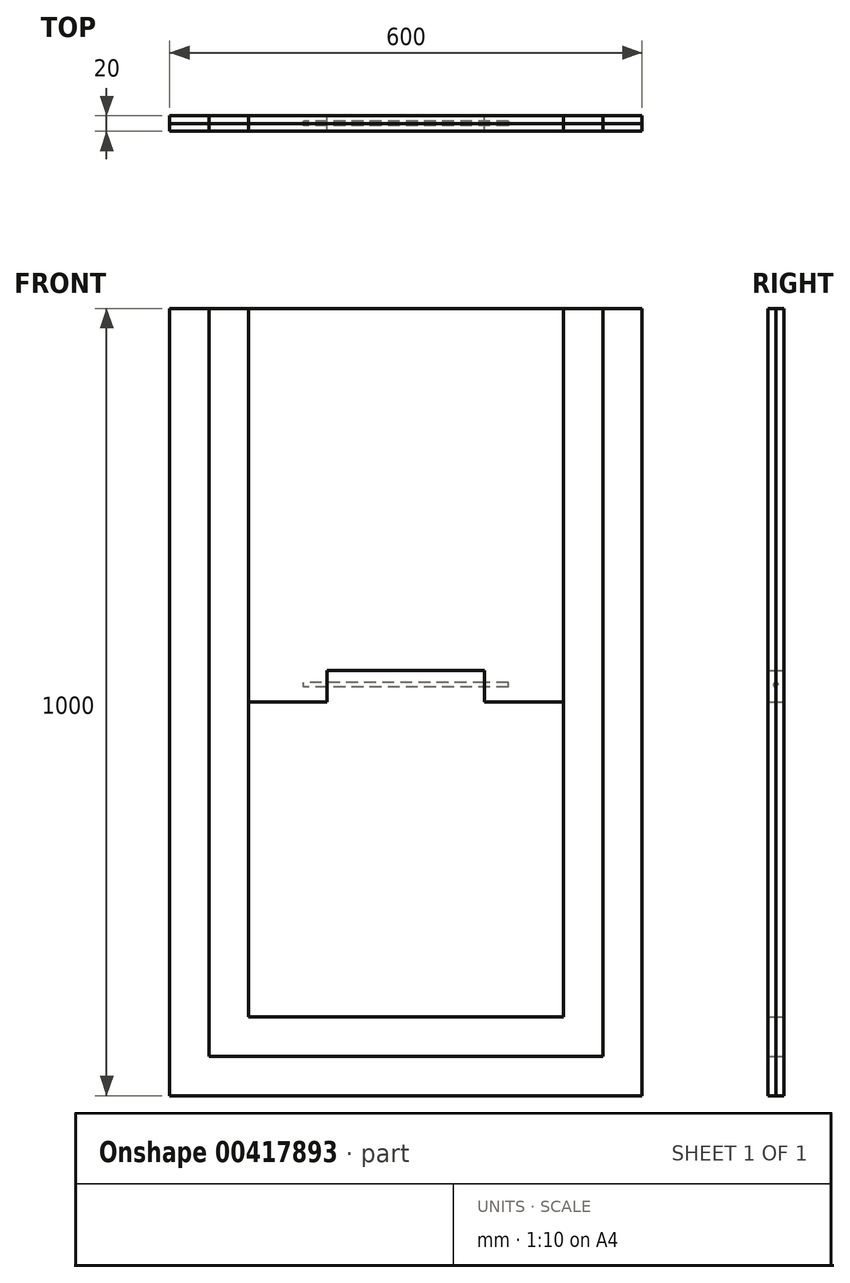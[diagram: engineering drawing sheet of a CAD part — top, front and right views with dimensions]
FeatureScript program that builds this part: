
annotation { "Feature Type Name" : "Feature", "Feature Type Description" : "" }
export const myFeature = defineFeature(function(context is Context, id is Id, definition is map)
    precondition{}
    {
        {
            var Q0;
            Q0=qCreatedBy(makeId("Front.planeOp"),FACE);
            var sketch = newSketch(context, id + "F0", { "sketchPlane" : qUnion([Q0])});
            skLineSegment(sketch, "E0", {"start": v(0, 0) * mm, "end": v(0, 1000) * mm});
            skLineSegment(sketch, "E1", {"start": v(0, 1000) * mm, "end": v(50, 1000) * mm});
            skLineSegment(sketch, "E2", {"start": v(50, 1000) * mm, "end": v(50, 50) * mm});
            skLineSegment(sketch, "E3", {"start": v(50, 50) * mm, "end": v(550, 50) * mm});
            skLineSegment(sketch, "E4", {"start": v(550, 50) * mm, "end": v(550, 1000) * mm});
            skLineSegment(sketch, "E5", {"start": v(550, 1000) * mm, "end": v(600, 1000) * mm});
            skLineSegment(sketch, "E6", {"start": v(600, 1000) * mm, "end": v(600, 0) * mm});
            skLineSegment(sketch, "E7", {"start": v(600, 0) * mm, "end": v(0, 0) * mm});
            skSolve(sketch);
        }
        {
            var Q0;
            Q0=qCreatedBy(makeId("Front.planeOp"),FACE);
            var sketch = newSketch(context, id + "F1", { "sketchPlane" : qUnion([Q0])});
            skLineSegment(sketch, "E8", {"start": v(50, 1000) * mm, "end": v(50, 50) * mm});
            skLineSegment(sketch, "E9", {"start": v(50, 50) * mm, "end": v(550, 50) * mm});
            skLineSegment(sketch, "E10", {"start": v(550, 50) * mm, "end": v(550, 1000) * mm});
            skLineSegment(sketch, "E11", {"start": v(550, 1000) * mm, "end": v(500, 1000) * mm});
            skLineSegment(sketch, "E12", {"start": v(500, 1000) * mm, "end": v(500, 100) * mm});
            skLineSegment(sketch, "E13", {"start": v(500, 100) * mm, "end": v(100, 100) * mm});
            skLineSegment(sketch, "E14", {"start": v(100, 100) * mm, "end": v(100, 1000) * mm});
            skLineSegment(sketch, "E15", {"start": v(100, 1000) * mm, "end": v(50, 1000) * mm});
            skSolve(sketch);
        }
        {
            var Q0;
            Q0=qCreatedBy(makeId("Front.planeOp"),FACE);
            var sketch = newSketch(context, id + "F2", { "sketchPlane" : qUnion([Q0])});
            skLineSegment(sketch, "E16", {"start": v(100, 1000) * mm, "end": v(100, 500) * mm});
            skLineSegment(sketch, "E17", {"start": v(100, 500) * mm, "end": v(200, 500) * mm});
            skLineSegment(sketch, "E18", {"start": v(200, 540) * mm, "end": v(400, 540) * mm});
            skLineSegment(sketch, "E19", {"start": v(400, 500) * mm, "end": v(500, 500) * mm});
            skLineSegment(sketch, "E20", {"start": v(500, 500) * mm, "end": v(500, 1000) * mm});
            skLineSegment(sketch, "E21", {"start": v(500, 1000) * mm, "end": v(100, 1000) * mm});
            skLineSegment(sketch, "E22", {"start": v(200, 500) * mm, "end": v(200, 540) * mm});
            skLineSegment(sketch, "E23", {"start": v(400, 500) * mm, "end": v(400, 540) * mm});
            skLineSegment(sketch, "E24", {"start": v(300, 611.08) * mm, "end": v(300, 468.28) * mm, "construction": true});
            skSolve(sketch);
        }
        {
            var Q0;
            Q0=qCreatedBy(makeId("Front.planeOp"),FACE);
            var sketch = newSketch(context, id + "F3", { "sketchPlane" : qUnion([Q0])});
            skLineSegment(sketch, "E25", {"start": v(200, 460) * mm, "end": v(200, 500) * mm, "construction": true});
            skLineSegment(sketch, "E26", {"start": v(200, 500) * mm, "end": v(100, 500) * mm});
            skLineSegment(sketch, "E27", {"start": v(100, 500) * mm, "end": v(100, 100) * mm});
            skLineSegment(sketch, "E28", {"start": v(100, 100) * mm, "end": v(500, 100) * mm});
            skLineSegment(sketch, "E29", {"start": v(500, 100) * mm, "end": v(500, 500) * mm});
            skLineSegment(sketch, "E30", {"start": v(500, 500) * mm, "end": v(400, 500) * mm});
            skLineSegment(sketch, "E31", {"start": v(400, 500) * mm, "end": v(400, 460) * mm, "construction": true});
            skLineSegment(sketch, "E32", {"start": v(400, 460) * mm, "end": v(200, 460) * mm, "construction": true});
            skLineSegment(sketch, "E33", {"start": v(300, 460) * mm, "end": v(300, 536.5) * mm, "construction": true});
            skLineSegment(sketch, "E34", {"start": v(200, 498) * mm, "end": v(400, 498) * mm, "construction": true});
            skLineSegment(sketch, "E35", {"start": v(200, 478) * mm, "end": v(400, 478) * mm, "construction": true});
            skLineSegment(sketch, "E36.MirrorCS", {"start": v(200, 522) * mm, "end": v(480, 522) * mm, "construction": true});
            skLineSegment(sketch, "E37.MirrorCS", {"start": v(200, 502) * mm, "end": v(400, 502) * mm, "construction": true});
            skLineSegment(sketch, "E38.MirrorCS", {"start": v(400, 500) * mm, "end": v(400, 540) * mm});
            skLineSegment(sketch, "E39.MirrorCS", {"start": v(400, 540) * mm, "end": v(200, 540) * mm});
            skLineSegment(sketch, "E40.MirrorCS", {"start": v(200, 540) * mm, "end": v(200, 500) * mm});
            skSolve(sketch);
        }
        {
            var Q0;
            Q0 = qSketchRegion(id + "F0", true);
            extrude(context, id + "F4", {"entities" : qUnion([Q0]), "depth" : 10 * mm});
        }
        {
            var Q0;
            Q0=makeQuery(id+"F4.opExtrude","CAP_FACE",FACE,{"disambiguationData":[OSD([sQuery(id+"F0.wireOp",EDGE,"E0"),sQuery(id+"F0.wireOp",EDGE,"E1"),sQuery(id+"F0.wireOp",EDGE,"E2"),sQuery(id+"F0.wireOp",EDGE,"E3"),sQuery(id+"F0.wireOp",EDGE,"E4"),sQuery(id+"F0.wireOp",EDGE,"E5"),sQuery(id+"F0.wireOp",EDGE,"E6"),sQuery(id+"F0.wireOp",EDGE,"E7")])],"isStart":false});
            var Q1;
            Q1 = qSketchRegion(id + "F0", true);
            extrude(context, id + "F5", {"entities" : qUnion([Q0, Q1]), "depth" : 10 * mm});
        }
        {
            var Q0;
            Q0=makeQuery(id+"F1.imprint","IMPRINT",FACE,{"disambiguationData":[TD([[makeQuery(id+"F1.imprint","IMPRINT",EDGE,{"derivedFrom":sQuery(id+"F1.wireOp",EDGE,"E8")}),1.0]])]});
            extrude(context, id + "F6", {"entities" : qUnion([Q0]), "depth" : 10 * mm});
        }
        {
            var Q0;
            Q0=makeQuery(id+"F6.opExtrude","CAP_FACE",FACE,{"disambiguationData":[OSD([sQuery(id+"F1.wireOp",EDGE,"E8"),sQuery(id+"F1.wireOp",EDGE,"E9"),sQuery(id+"F1.wireOp",EDGE,"E10"),sQuery(id+"F1.wireOp",EDGE,"E11"),sQuery(id+"F1.wireOp",EDGE,"E12"),sQuery(id+"F1.wireOp",EDGE,"E13"),sQuery(id+"F1.wireOp",EDGE,"E14"),sQuery(id+"F1.wireOp",EDGE,"E15")])],"isStart":false});
            extrude(context, id + "F7", {"entities" : qUnion([Q0]), "depth" : 10 * mm});
        }
        {
            var Q0;
            Q0 = qSketchRegion(id + "F2", true);
            extrude(context, id + "F8", {"entities" : qUnion([Q0]), "depth" : 10 * mm});
        }
        {
            var Q0;
            Q0=makeQuery(id+"F8.opExtrude","CAP_FACE",FACE,{"disambiguationData":[OSD([sQuery(id+"F2.wireOp",EDGE,"E16"),sQuery(id+"F2.wireOp",EDGE,"E17"),sQuery(id+"F2.wireOp",EDGE,"RWHdpN4b-uQmZ-eVFq-R4nj-n3kl5uwec7N7"),sQuery(id+"F2.wireOp",EDGE,"E18"),sQuery(id+"F2.wireOp",EDGE,"KOj6WaeH-bQeP-T0in-QHYA-rBpoyiClq4G4"),sQuery(id+"F2.wireOp",EDGE,"E19"),sQuery(id+"F2.wireOp",EDGE,"E20"),sQuery(id+"F2.wireOp",EDGE,"E21")])],"isStart":false});
            extrude(context, id + "F9", {"entities" : qUnion([Q0]), "depth" : 10 * mm});
        }
        {
            var Q0;
            Q0 = qSketchRegion(id + "F3", true);
            extrude(context, id + "F10", {"entities" : qUnion([Q0]), "depth" : 10 * mm});
        }
        {
            var Q0;
            Q0=makeQuery(id+"F10.opExtrude","CAP_FACE",FACE,{"disambiguationData":[OSD([sQuery(id+"F3.wireOp",EDGE,"E25"),sQuery(id+"F3.wireOp",EDGE,"E26"),sQuery(id+"F3.wireOp",EDGE,"E27"),sQuery(id+"F3.wireOp",EDGE,"E28"),sQuery(id+"F3.wireOp",EDGE,"E29"),sQuery(id+"F3.wireOp",EDGE,"E30"),sQuery(id+"F3.wireOp",EDGE,"E31"),sQuery(id+"F3.wireOp",EDGE,"E32")])],"isStart":false});
            extrude(context, id + "F11", {"entities" : qUnion([Q0]), "depth" : 10 * mm});
        }
        {
            var Q0;
            Q0=qCreatedBy(makeId("Right.planeOp"),FACE);
            var sketch = newSketch(context, id + "F12", { "sketchPlane" : qUnion([Q0])});
            skCircle(sketch, "E41", {"center": v(-10, 522) * mm, "radius": 3 * mm});
            skSolve(sketch);
        }
        {
            var Q0;
            Q0 = qSketchRegion(id + "F12", true);
            extrude(context, id + "F13", {"entities" : qUnion([Q0]), "depth" : 260 * mm});
        }
        {
            var Q0;
            Q0=makeQuery(id+"F13.opExtrude","SWEPT_BODY",BODY,{"disambiguationData":[OSD([sQuery(id+"F12.wireOp",EDGE,"E41")])]});
            var Q1;
            Q1=sQuery(id+"F3.wireOp",EDGE,"E36.MirrorCS");
            transform(context, id + "F14", {"entities" : qUnion([Q0]), "transformType" : TransformType.TRANSLATION_DISTANCE, "transformDirection" : qUnion([Q1]), "distance" : 170 * mm, "makeCopy" : false});
        }
    });
